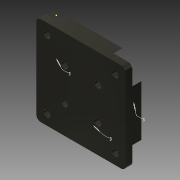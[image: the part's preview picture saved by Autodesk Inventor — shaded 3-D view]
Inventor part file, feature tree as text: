
AUTODESK INVENTOR PART (.ipt)
format: ipt  version: 2015 (Build 190159000, 159)  size: 166,912 bytes
history: native  units: mm
features: sketch x2, extrude x2, fillet x1
ambient origin geometry x8: Origin, YZ Plane, XZ Plane, XY Plane, X Axis, Y Axis, Z Axis, Center Point
bodies: Body1 (feature_tree)
feature tree (5):
  sketch  "Sketch1"  dims[d0=36.0mm]
  extrude  "Extrusion5"  Depth=3.0mm TaperAngle=0.0deg
  extrude  "Extrusion6"  Depth=7.0mm TaperAngle=0.0deg
  fillet  "Fillet2"  Radius=2.0mm
  sketch  "Sketch2"  dims[d55=36.0mm d56=40.0mm d57=40.0mm d58=3.0mm d59=3.0mm d60=3.0mm d61=3.0mm d62=3.0mm d63=0.0mm d64=7.0mm d65=0.0mm d66=2.0mm d68=3.0mm d71=3.0mm d72=3.0mm]
